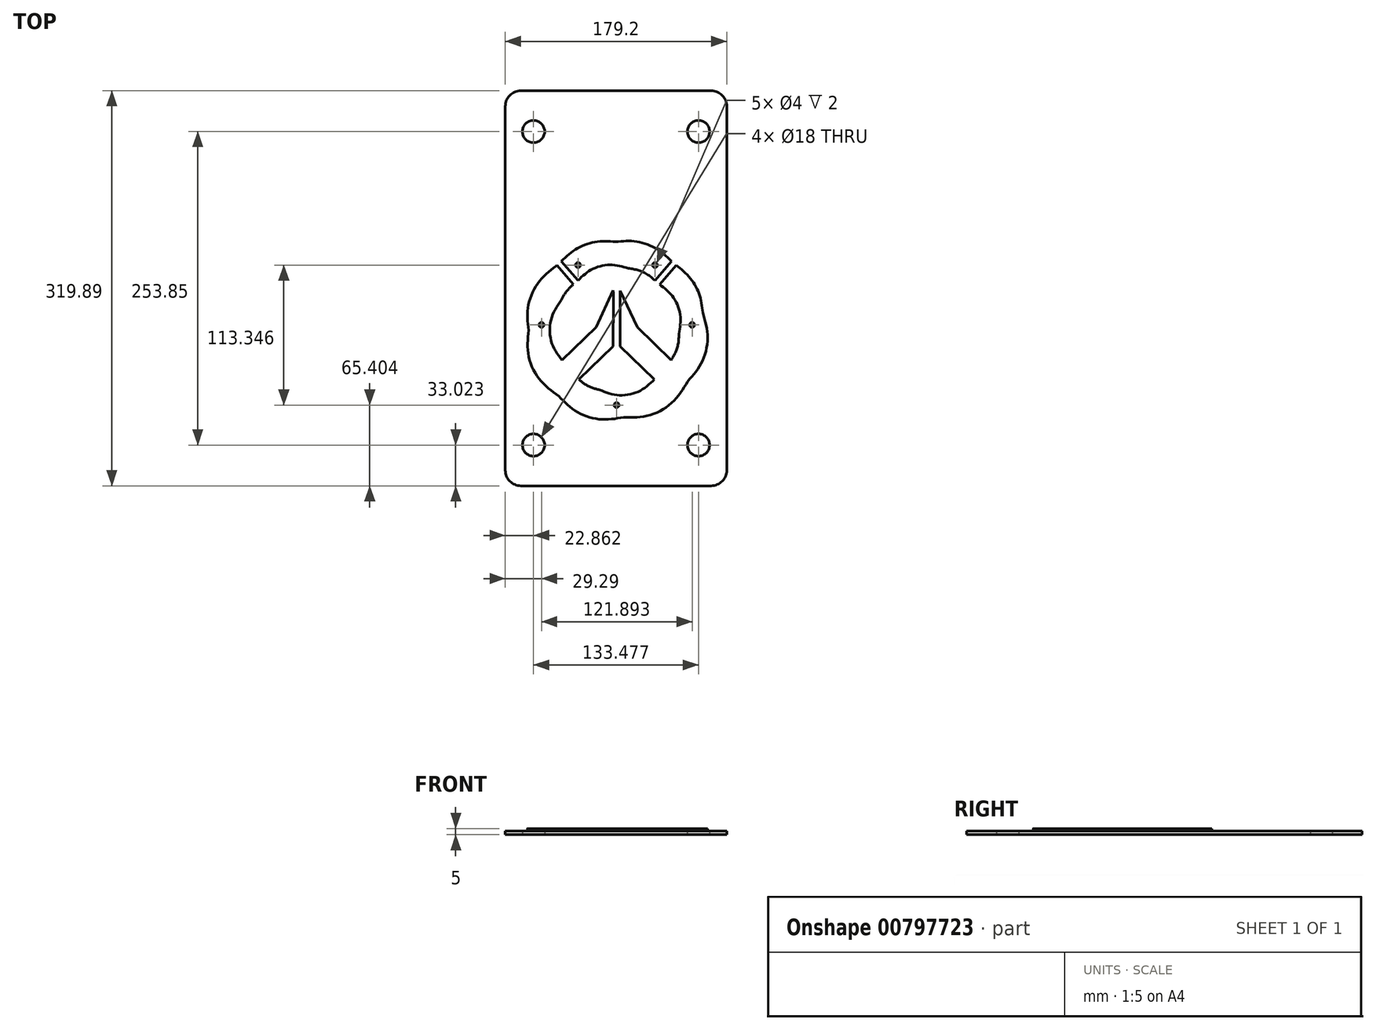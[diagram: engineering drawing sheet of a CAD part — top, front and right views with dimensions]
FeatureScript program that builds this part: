
annotation { "Feature Type Name" : "Feature", "Feature Type Description" : "" }
export const myFeature = defineFeature(function(context is Context, id is Id, definition is map)
    precondition{}
    {
        {
            var Q0;
            Q0=qCreatedBy(makeId("Top.planeOp"),FACE);
            var sketch = newSketch(context, id + "F0", { "sketchPlane" : qUnion([Q0])});
            skFitSpline(sketch, "E0", {"points": [v(-0.85, 67.32) * mm, v(-16.7, 67.21) * mm, v(-32.36, 61.57) * mm, v(-44.66, 51.63) * mm]});
            skFitSpline(sketch, "E1", {"points": [v(-31.22, 36.02) * mm, v(-19.87, 44.98) * mm, v(-4.58, 48.63) * mm, v(9.6, 45.8) * mm]});
            skFitSpline(sketch, "E2", {"points": [v(9.6, 45.8) * mm, v(17.4, 44.3) * mm, v(24.82, 40.89) * mm, v(31.08, 36.02) * mm]});
            skLineSegment(sketch, "E3", {"start": v(-44.66, 51.63) * mm, "end": v(-31.22, 36.02) * mm});
            skFitSpline(sketch, "E4", {"points": [v(44.52, 51.63) * mm, v(31.8, 61.9) * mm, v(15.54, 67.56) * mm, v(-0.85, 67.32) * mm]});
            skLineSegment(sketch, "E5", {"start": v(31.08, 36.02) * mm, "end": v(44.52, 51.63) * mm});
            skFitSpline(sketch, "E6", {"points": [v(-49.04, 47.8) * mm, v(-63.2, 34.49) * mm, v(-71.52, 15.14) * mm, v(-71.25, -4.38) * mm]});
            skFitSpline(sketch, "E7", {"points": [v(-71.25, -4.38) * mm, v(-71.25, -24.64) * mm, v(-62, -44.54) * mm, v(-46.66, -57.7) * mm]});
            skFitSpline(sketch, "E8", {"points": [v(-46.66, -57.7) * mm, v(-32.47, -70.11) * mm, v(-13.17, -76.44) * mm, v(5.66, -74.84) * mm]});
            skFitSpline(sketch, "E9", {"points": [v(5.66, -74.84) * mm, v(26.08, -73.32) * mm, v(45.45, -62.41) * mm, v(57.43, -45.85) * mm]});
            skFitSpline(sketch, "E10", {"points": [v(57.43, -45.85) * mm, v(69.09, -30.1) * mm, v(73.65, -9.35) * mm, v(69.78, 9.9) * mm]});
            skFitSpline(sketch, "E11", {"points": [v(69.78, 9.9) * mm, v(66.94, 24.63) * mm, v(59.21, 38.29) * mm, v(48.23, 48.44) * mm]});
            skFitSpline(sketch, "E12", {"points": [v(34.78, 32.83) * mm, v(45.61, 22.61) * mm, v(51.53, 7.54) * mm, v(50.41, -7.33) * mm]});
            skFitSpline(sketch, "E13", {"points": [v(50.41, -7.33) * mm, v(49.93, -14.7) * mm, v(47.79, -21.97) * mm, v(44.17, -28.44) * mm]});
            skLineSegment(sketch, "E14", {"start": v(48.23, 48.44) * mm, "end": v(34.78, 32.83) * mm});
            skFitSpline(sketch, "E15", {"points": [v(30.61, -44.1) * mm, v(18.27, -53.7) * mm, v(1.34, -56.87) * mm, v(-13.67, -52.62) * mm]});
            skFitSpline(sketch, "E16", {"points": [v(-13.67, -52.62) * mm, v(-19.77, -50.92) * mm, v(-25.56, -48.06) * mm, v(-30.59, -44.22) * mm]});
            skLineSegment(sketch, "E17", {"start": v(44.17, -28.44) * mm, "end": v(16.77, -1.97) * mm});
            skLineSegment(sketch, "E18", {"start": v(16.77, -1.97) * mm, "end": v(2.94, 27.83) * mm});
            skLineSegment(sketch, "E19", {"start": v(2.94, 27.83) * mm, "end": v(2.92, -17.3) * mm});
            skLineSegment(sketch, "E20", {"start": v(2.92, -17.3) * mm, "end": v(30.61, -44.1) * mm});
            skFitSpline(sketch, "E21", {"points": [v(-2.7, -17.3) * mm, v(-2.75, -2.63) * mm, v(-2.54, 13.2) * mm, v(-2.7, 27.88) * mm]});
            skLineSegment(sketch, "E22", {"start": v(-30.59, -44.22) * mm, "end": v(-2.7, -17.3) * mm});
            skFitSpline(sketch, "E23", {"points": [v(-44.2, -28.66) * mm, v(-52.62, -13.94) * mm, v(-52.83, 5.09) * mm, v(-44.7, 19.97) * mm]});
            skFitSpline(sketch, "E24", {"points": [v(-44.7, 19.97) * mm, v(-42.17, 24.74) * mm, v(-38.81, 29.09) * mm, v(-34.92, 32.83) * mm]});
            skLineSegment(sketch, "E25", {"start": v(-2.7, 27.88) * mm, "end": v(-16.55, -1.97) * mm});
            skLineSegment(sketch, "E26", {"start": v(-16.55, -1.97) * mm, "end": v(-44.2, -28.66) * mm});
            skFitSpline(sketch, "E27", {"points": [v(-48.37, 48.44) * mm, v(-48.6, 48.23) * mm, v(-48.82, 48.01) * mm, v(-49.04, 47.8) * mm]});
            skLineSegment(sketch, "E28", {"start": v(-34.92, 32.83) * mm, "end": v(-48.37, 48.44) * mm});
            skPoint(sketch, "E29", {"position": v(0, -75.08) * mm});
            skCircle(sketch, "E30", {"center": v(-31.22, 48.44) * mm, "radius": 2 * mm});
            skCircle(sketch, "E31", {"center": v(31.08, 48.44) * mm, "radius": 2 * mm});
            skCircle(sketch, "E32", {"center": v(0, -64.9) * mm, "radius": 2 * mm});
            skCircle(sketch, "E33", {"center": v(-60.77, 0) * mm, "radius": 2 * mm});
            skCircle(sketch, "E34", {"center": v(61.12, 0) * mm, "radius": 2 * mm});
            skSolve(sketch);
        }
        {
            var Q0;
            Q0=qCreatedBy(makeId("Top.planeOp"),FACE);
            var sketch = newSketch(context, id + "F1", { "sketchPlane" : qUnion([Q0])});
            skLineSegment(sketch, "E35.bottom", {"start": v(89.14, -117.6) * mm, "end": v(89.14, 176.88) * mm});
            skLineSegment(sketch, "E35.top", {"start": v(-90.06, -117.6) * mm, "end": v(-90.06, 176.88) * mm});
            skLineSegment(sketch, "E35.left", {"start": v(76.44, -130.3) * mm, "end": v(-77.36, -130.3) * mm});
            skLineSegment(sketch, "E35.right", {"start": v(76.44, 189.58) * mm, "end": v(-77.36, 189.58) * mm});
            skCircle(sketch, "E36", {"center": v(-67.2, -97.29) * mm, "radius": 9 * mm});
            skCircle(sketch, "E37", {"center": v(66.28, -97.29) * mm, "radius": 9 * mm});
            skCircle(sketch, "E38", {"center": v(-67.2, 156.56) * mm, "radius": 9 * mm});
            skCircle(sketch, "E39", {"center": v(66.28, 156.56) * mm, "radius": 9 * mm});
            skPoint(sketch, "E40.visualSharp", {"position": v(-90.06, -130.3) * mm});
            skArc(sketch, "E40.filletArc", {"start": v(-90.06, -117.6) * mm, "mid": v(-86.34, -126.59) * mm, "end": v(-77.36, -130.3) * mm});
            skPoint(sketch, "E41.visualSharp", {"position": v(-90.06, 189.58) * mm});
            skArc(sketch, "E41.filletArc", {"start": v(-77.36, 189.58) * mm, "mid": v(-86.34, 185.86) * mm, "end": v(-90.06, 176.88) * mm});
            skPoint(sketch, "E42.visualSharp", {"position": v(89.14, -130.3) * mm});
            skArc(sketch, "E42.filletArc", {"start": v(76.44, -130.3) * mm, "mid": v(85.42, -126.59) * mm, "end": v(89.14, -117.6) * mm});
            skPoint(sketch, "E43.visualSharp", {"position": v(89.14, 189.58) * mm});
            skArc(sketch, "E43.filletArc", {"start": v(89.14, 176.88) * mm, "mid": v(85.42, 185.86) * mm, "end": v(76.44, 189.58) * mm});
            skPoint(sketch, "E44", {"position": v(-0.46, -130.3) * mm});
            skPoint(sketch, "E45", {"position": v(-0.46, 189.58) * mm});
            skPoint(sketch, "E46", {"position": v(-90.06, 29.64) * mm});
            skPoint(sketch, "E47", {"position": v(89.14, 29.64) * mm});
            skSolve(sketch);
        }
        {
            var Q0;
            Q0 = qSketchRegion(id + "F1", true);
            extrude(context, id + "F2", {"entities" : qUnion([Q0]), "depth" : 3 * mm, "offsetDistance" : 25.4 * mm});
        }
        {
            var Q0;
            Q0=makeQuery(id+"F0.imprint","IMPRINT",FACE,{"disambiguationData":[TD([[makeQuery(id+"F0.imprint","IMPRINT",EDGE,{"derivedFrom":sQuery(id+"F0.wireOp",EDGE,"E0")}),1.0]])]});
            extrude(context, id + "F3", {"entities" : qUnion([Q0]), "operationType" : NewBodyOperationType.ADD, "depth" : 5 * mm, "offsetDistance" : 25.4 * mm});
        }
        {
            var Q0;
            Q0=makeQuery(id+"F0.imprint","IMPRINT",FACE,{"disambiguationData":[TD([[makeQuery(id+"F0.imprint","IMPRINT",EDGE,{"derivedFrom":sQuery(id+"F0.wireOp",EDGE,"E6")}),1.0]])]});
            extrude(context, id + "F4", {"entities" : qUnion([Q0]), "operationType" : NewBodyOperationType.ADD, "depth" : 5 * mm, "offsetDistance" : 25.4 * mm});
        }
    });
